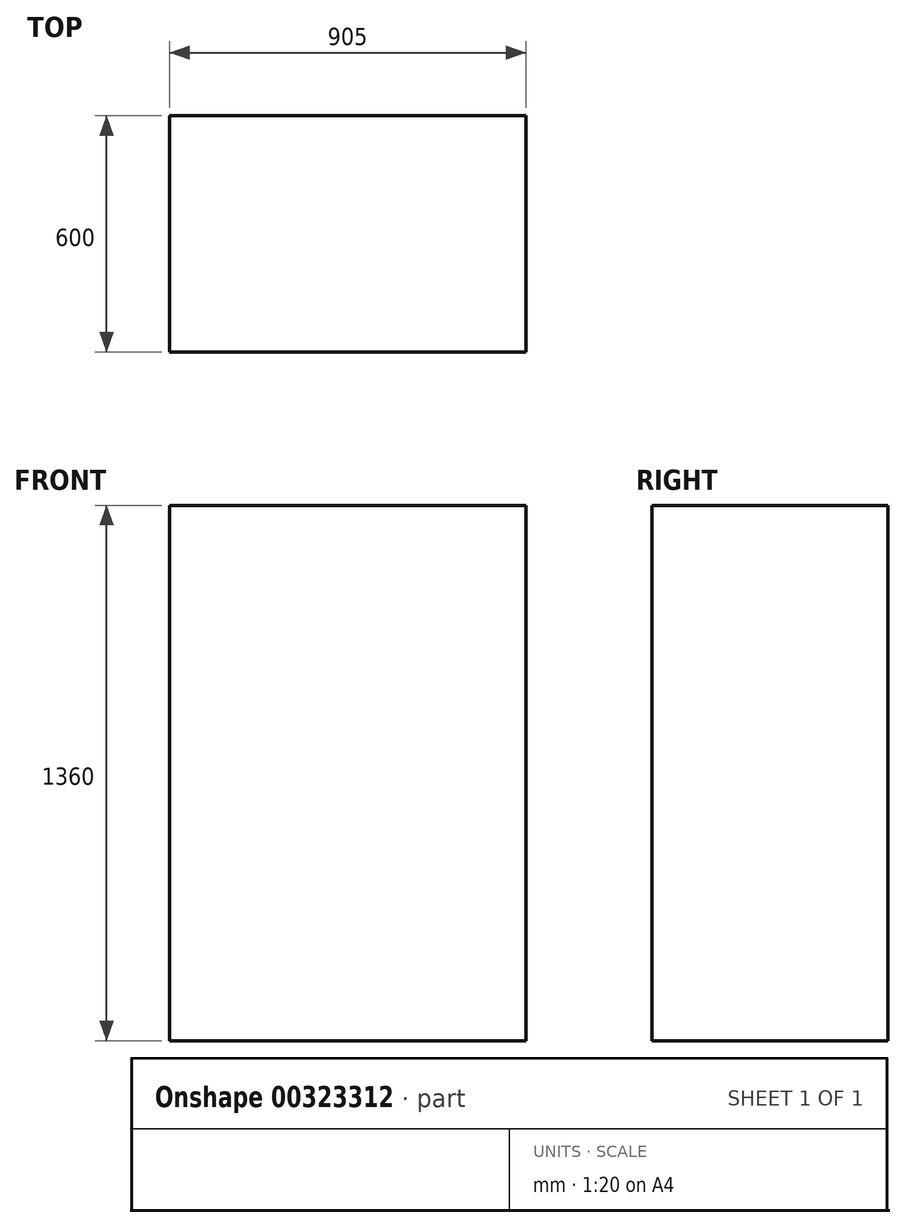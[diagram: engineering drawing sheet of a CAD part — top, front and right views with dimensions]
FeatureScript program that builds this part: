
annotation { "Feature Type Name" : "Feature", "Feature Type Description" : "" }
export const myFeature = defineFeature(function(context is Context, id is Id, definition is map)
    precondition{}
    {
        {
            var Q0;
            Q0=qCreatedBy(makeId("Front.planeOp"),FACE);
            var sketch = newSketch(context, id + "F0", { "sketchPlane" : qUnion([Q0])});
            skLineSegment(sketch, "E0.bottom", {"start": v(0, 0) * mm, "end": v(905, 0) * mm});
            skLineSegment(sketch, "E0.top", {"start": v(0, 1360) * mm, "end": v(905, 1360) * mm});
            skLineSegment(sketch, "E0.left", {"start": v(0, 0) * mm, "end": v(0, 1360) * mm});
            skLineSegment(sketch, "E0.right", {"start": v(905, 0) * mm, "end": v(905, 1360) * mm});
            skSolve(sketch);
        }
        {
            var Q0;
            Q0 = qSketchRegion(id + "F0", true);
            extrude(context, id + "F1", {"entities" : qUnion([Q0]), "depth" : 600 * mm});
        }
    });
